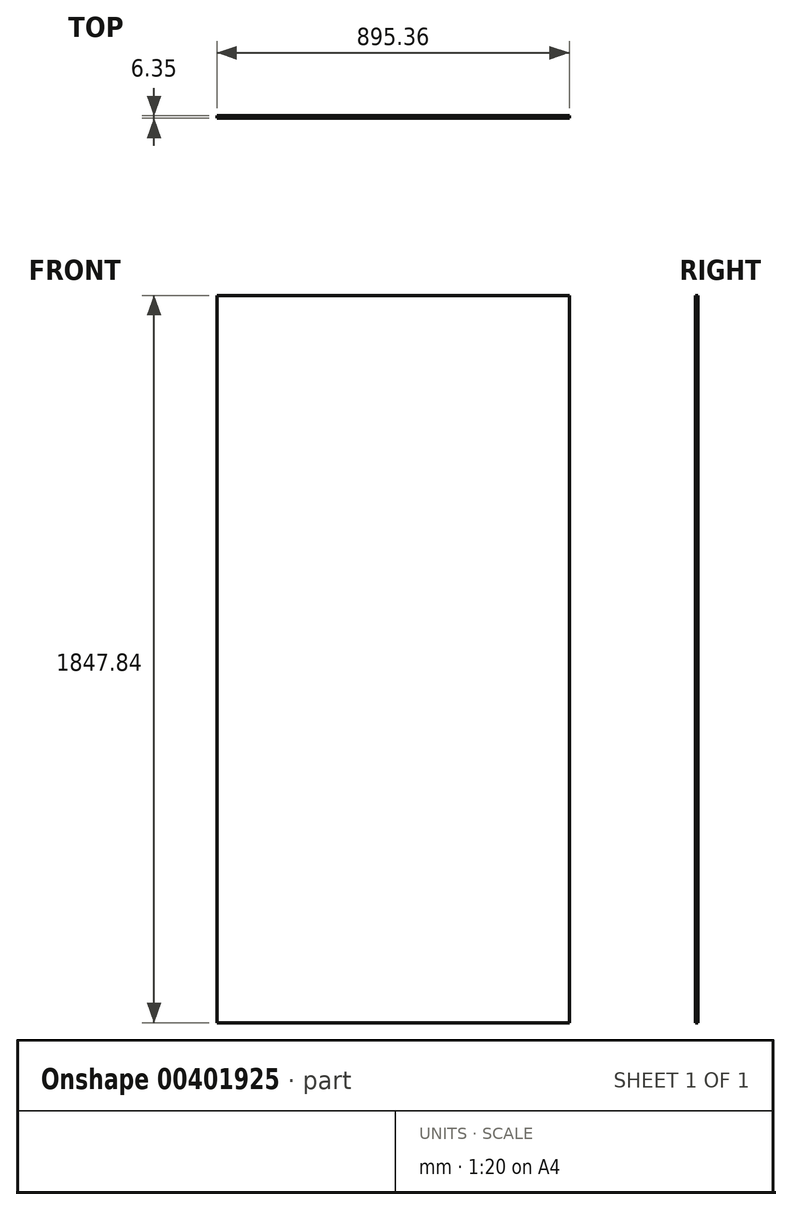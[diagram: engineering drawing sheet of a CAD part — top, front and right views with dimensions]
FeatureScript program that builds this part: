
annotation { "Feature Type Name" : "Feature", "Feature Type Description" : "" }
export const myFeature = defineFeature(function(context is Context, id is Id, definition is map)
    precondition{}
    {
        {
            var Q0;
            Q0=qCreatedBy(makeId("Front.planeOp"),FACE);
            var sketch = newSketch(context, id + "F0", { "sketchPlane" : qUnion([Q0])});
            skLineSegment(sketch, "E0.bottom", {"start": v(447.68, 923.93) * mm, "end": v(-447.67, 923.93) * mm});
            skLineSegment(sketch, "E0.top", {"start": v(447.67, -923.93) * mm, "end": v(-447.68, -923.93) * mm});
            skLineSegment(sketch, "E0.left", {"start": v(447.68, 923.93) * mm, "end": v(447.67, -923.93) * mm});
            skLineSegment(sketch, "E0.right", {"start": v(-447.67, 923.93) * mm, "end": v(-447.68, -923.93) * mm});
            skPoint(sketch, "E0.middle", {"position": v(0, 0) * mm});
            skSolve(sketch);
        }
        {
            var Q0;
            Q0=qSketchRegion(id+"F0",true);
            extrude(context, id + "F1", {"entities" : qUnion([Q0]), "depth" : 6.35 * mm});
        }
    });
